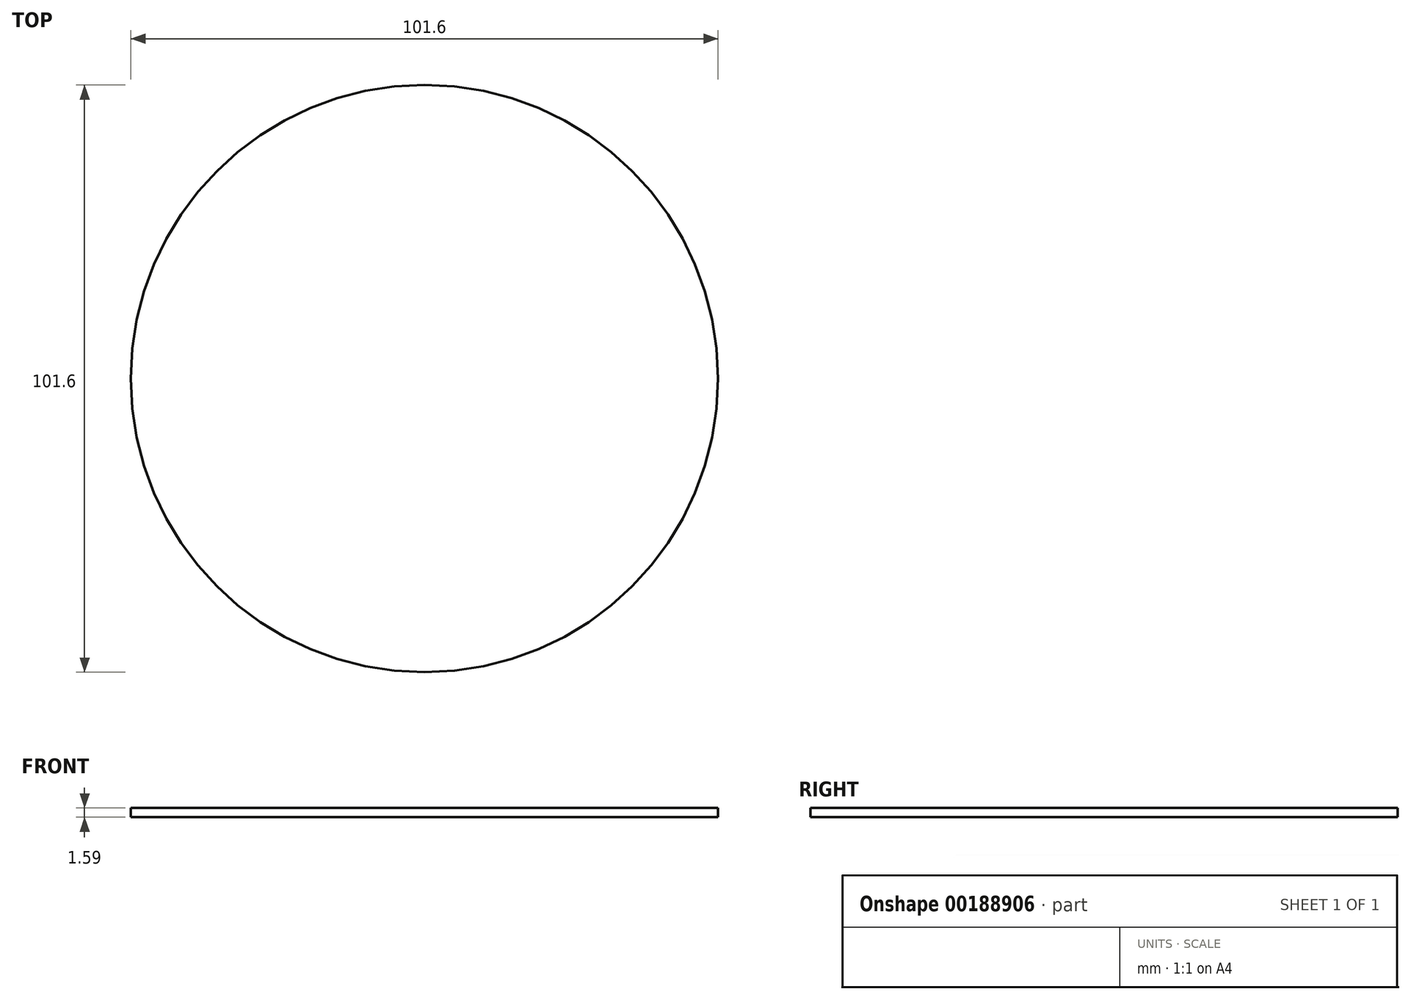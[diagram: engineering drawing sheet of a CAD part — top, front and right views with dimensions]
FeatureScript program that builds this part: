
annotation { "Feature Type Name" : "Feature", "Feature Type Description" : "" }
export const myFeature = defineFeature(function(context is Context, id is Id, definition is map)
    precondition{}
    {
        {
            var Q0;
            Q0=qCreatedBy(makeId("Top.planeOp"),FACE);
            var sketch = newSketch(context, id + "F0", { "sketchPlane" : qUnion([Q0])});
            skCircle(sketch, "E0", {"center": v(0, 0) * mm, "radius": 50.8 * mm});
            skSolve(sketch);
        }
        {
            var Q0;
            Q0=qSketchRegion(id+"F0",true);
            extrude(context, id + "F1", {"entities" : qUnion([Q0]), "depth" : 1.59 * mm});
        }
    });
